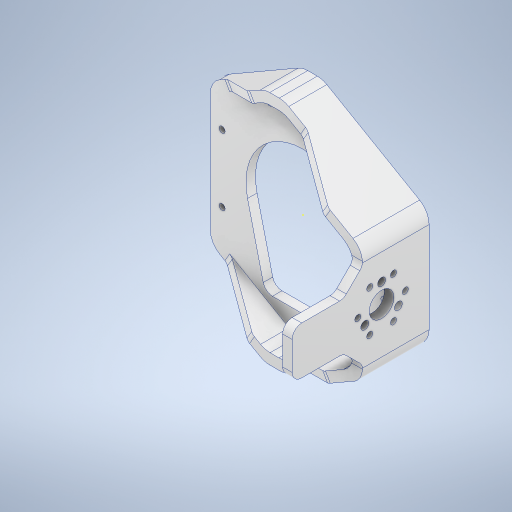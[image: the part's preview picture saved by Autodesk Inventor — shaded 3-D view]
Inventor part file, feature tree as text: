
AUTODESK INVENTOR PART (.ipt)
format: ipt  version: 2024.3 (Build 283343000, 343)  size: 762,368 bytes
history: native  units: mm
features: sketch x18, extrude x14, fillet x4, hole x3, projected_geometry x3, other x1
ambient origin geometry x8: Origin, YZ Plane, XZ Plane, XY Plane, X Axis, Y Axis, Z Axis, Center Point
bodies: Body1 (feature_tree)
feature tree (43):
  other  "ソリッド1"
  extrude  "押し出し1"  Depth=5.0mm TaperAngle=0.0deg
  hole  "穴1"  [1 undecoded]
  extrude  "押し出し2"  TaperAngle=22.5deg  [1 undecoded]
  extrude  "押し出し13"  Depth=80.0mm TaperAngle=360.0deg
  hole  "穴5"  [1 undecoded]
  hole  "穴6"  [1 undecoded]
  extrude  "押し出し14"  Depth=50.0mm
  extrude  "押し出し21"  Depth=65.0mm
  sketch  "スケッチ35"
  extrude  "押し出し28"  Depth=60.0mm TaperAngle=360.0deg
  extrude  "押し出し31"  Depth=65.0mm
  extrude  "押し出し32"  Depth=50.0mm
  extrude  "押し出し33"  Depth=65.0mm
  extrude  "押し出し34"  Depth=5.0mm TaperAngle=0.0deg
  extrude  "押し出し35"  Depth=60.0mm TaperAngle=360.0deg
  fillet  "フィレット28"  Radius=25.0mm
  fillet  "フィレット29"  [1 undecoded]
  extrude  "押し出し36"  Depth=30.0mm TaperAngle=360.0deg
  extrude  "押し出し37"  Depth=25.0mm
  extrude  "押し出し38"  TaperAngle=0.0deg  [1 undecoded]
  fillet  "フィレット32"  Radius=13.0mm
  fillet  "フィレット33"  Radius=32.5mm
  sketch  "スケッチ1"
  sketch  "スケッチ2"
  sketch  "スケッチ3"
  sketch  "スケッチ17"
  sketch  "スケッチ18"
  sketch  "スケッチ19"
  sketch  "スケッチ20"
  sketch  "スケッチ28"
  sketch  "スケッチ36"
  projected_geometry  "投影ループ1"
  sketch  "スケッチ39"
  sketch  "スケッチ40"
  sketch  "スケッチ42"
  sketch  "スケッチ43"
  sketch  "スケッチ45"
  projected_geometry  "投影ループ2"
  sketch  "スケッチ46"
  projected_geometry  "投影ループ3"
  sketch  "スケッチ47"
  sketch  "スケッチ48"
note: 6 required parameter values undecoded (feature->parameter linkage not recoverable at this tier; creation-order binding heuristic only, values carry confidence <= 0.55)
